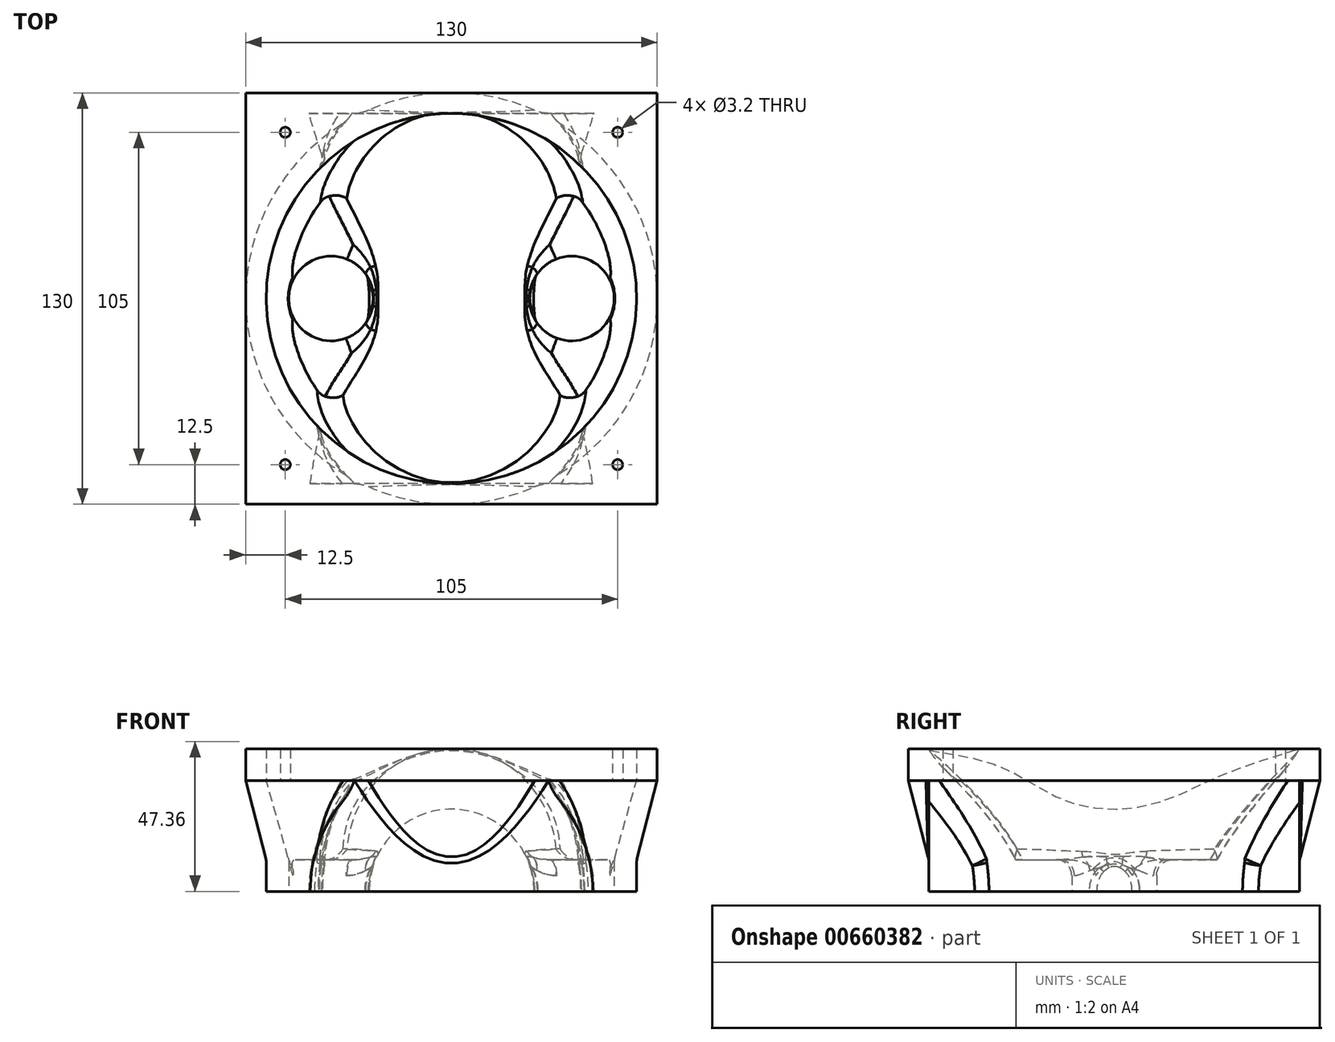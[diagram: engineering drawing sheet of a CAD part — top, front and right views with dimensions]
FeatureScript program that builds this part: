
annotation { "Feature Type Name" : "Feature", "Feature Type Description" : "" }
export const myFeature = defineFeature(function(context is Context, id is Id, definition is map)
    precondition{}
    {
        {
            var Q0;
            Q0=qCreatedBy(makeId("Front.planeOp"),FACE);
            var sketch = newSketch(context, id + "F0", { "sketchPlane" : qUnion([Q0])});
            skPoint(sketch, "E0", {"position": v(56, 0) * mm});
            skPoint(sketch, "E1", {"position": v(65, 35) * mm});
            skLineSegment(sketch, "E2", {"start": v(0, 10) * mm, "end": v(0, 35) * mm});
            skPoint(sketch, "E3", {"position": v(58.5, 35) * mm});
            skPoint(sketch, "E4", {"position": v(-21.4, 10) * mm});
            skLineSegment(sketch, "E5", {"start": v(51.4, 10) * mm, "end": v(53, 10) * mm});
            skLineSegment(sketch, "E6", {"start": v(53, 10) * mm, "end": v(53, 0) * mm});
            skLineSegment(sketch, "E7", {"start": v(58.5, 35) * mm, "end": v(65, 35) * mm});
            skPoint(sketch, "E8", {"position": v(53, 10) * mm});
            skLineSegment(sketch, "E9", {"start": v(58.5, 35) * mm, "end": v(51.4, 10) * mm});
            skLineSegment(sketch, "E10", {"start": v(53, 0) * mm, "end": v(56, 0) * mm});
            skLineSegment(sketch, "E11", {"start": v(65, 35) * mm, "end": v(56, 0) * mm});
            skPoint(sketch, "E12", {"position": v(51.4, 10) * mm});
            skPoint(sketch, "E13", {"position": v(21.4, 10) * mm});
            skLineSegment(sketch, "E14", {"start": v(21.4, 10) * mm, "end": v(23, 10) * mm});
            skCircle(sketch, "E15", {"center": v(0, 10) * mm, "radius": 23 * mm, "construction": true});
            skCircle(sketch, "E16", {"center": v(0, 10) * mm, "radius": 21.4 * mm, "construction": true});
            skLineSegment(sketch, "E17", {"start": v(23, 10) * mm, "end": v(23, 0) * mm});
            skLineSegment(sketch, "E18", {"start": v(23, 0) * mm, "end": v(0, 0) * mm});
            skArc(sketch, "E19", {"start": v(0, 31.4) * mm, "mid": v(15.13, 25.13) * mm, "end": v(21.4, 10) * mm});
            skLineSegment(sketch, "E20", {"start": v(0, 10) * mm, "end": v(0, 0) * mm});
            skLineSegment(sketch, "E21", {"start": v(23, 10) * mm, "end": v(51.4, 10) * mm, "construction": true});
            skPoint(sketch, "E22", {"position": v(37.2, 10) * mm});
            skCircle(sketch, "E23", {"center": v(37.2, 10) * mm, "radius": 14.2 * mm, "construction": true});
            skArc(sketch, "E24", {"start": v(23, 10) * mm, "mid": v(37.2, 24.2) * mm, "end": v(51.4, 10) * mm});
            skLineSegment(sketch, "E25", {"start": v(23, 0) * mm, "end": v(53, 0) * mm});
            skFitSpline(sketch, "E26", {"points": [v(58.5, 35) * mm, v(53.56, 28.48) * mm, v(37.2, 24.2) * mm], "startDerivative": vector(-8.81, -17.66) * mm, "endDerivative": vector(-32.37, -4.71) * mm});
            skSolve(sketch);
        }
        {
            var Q0;
            Q0=makeQuery(id+"F0.imprint","IMPRINT",FACE,{"disambiguationData":[TD([[makeQuery(id+"F0.imprint","IMPRINT",EDGE,{"derivedFrom":sQuery(id+"F0.wireOp",EDGE,"E5")}),1.0]])]});
            var Q1;
            Q1=sQuery(id+"F0.wireOp",EDGE,"E2");
            revolve(context, id + "F1", {"entities" : qUnion([Q0]), "axis" : qUnion([Q1]), "revolveType" : RevolveType.FULL});
        }
        {
            var Q0;
            Q0=qCreatedBy(makeId("Top.planeOp"),FACE);
            var sketch = newSketch(context, id + "F2", { "sketchPlane" : qUnion([Q0])});
            skLineSegment(sketch, "E27.bottom", {"start": v(-50, -12) * mm, "end": v(-26, -12) * mm, "construction": true});
            skLineSegment(sketch, "E27.top", {"start": v(-50, 12) * mm, "end": v(-26, 12) * mm, "construction": true});
            skLineSegment(sketch, "E27.left", {"start": v(-50, -12) * mm, "end": v(-50, 12) * mm, "construction": true});
            skLineSegment(sketch, "E27.right", {"start": v(-26, -12) * mm, "end": v(-26, 12) * mm, "construction": true});
            skLineSegment(sketch, "E28.bottom", {"start": v(-53, -15) * mm, "end": v(-23, -15) * mm});
            skLineSegment(sketch, "E28.top", {"start": v(-53, 15) * mm, "end": v(-23, 15) * mm});
            skLineSegment(sketch, "E28.left", {"start": v(-53, -15) * mm, "end": v(-53, 15) * mm});
            skLineSegment(sketch, "E28.right", {"start": v(-23, -15) * mm, "end": v(-23, 15) * mm});
            skCircle(sketch, "E29", {"center": v(-50, 12) * mm, "radius": 1.6 * mm});
            skCircle(sketch, "E30", {"center": v(-50, -12) * mm, "radius": 1.6 * mm});
            skCircle(sketch, "E31", {"center": v(-26, 12) * mm, "radius": 1.6 * mm});
            skCircle(sketch, "E32", {"center": v(-26, -12) * mm, "radius": 1.6 * mm});
            skCircle(sketch, "E33", {"center": v(-38, 0) * mm, "radius": 13.4 * mm});
            skLineSegment(sketch, "E34", {"start": v(0, 86.14) * mm, "end": v(13.4, 86.14) * mm});
            skLineSegment(sketch, "E35", {"start": v(0, 86.14) * mm, "end": v(0, 121.14) * mm});
            skLineSegment(sketch, "E36", {"start": v(0, 121.14) * mm, "end": v(60, 121.14) * mm});
            skLineSegment(sketch, "E37", {"start": v(13.4, 86.14) * mm, "end": v(60, 121.14) * mm});
            skLineSegment(sketch, "E38.bottom", {"start": v(-60, -60) * mm, "end": v(60, -60) * mm});
            skLineSegment(sketch, "E38.top", {"start": v(-60, 60) * mm, "end": v(60, 60) * mm});
            skLineSegment(sketch, "E38.left", {"start": v(-60, -60) * mm, "end": v(-60, 60) * mm});
            skLineSegment(sketch, "E38.right", {"start": v(60, -60) * mm, "end": v(60, 60) * mm});
            skLineSegment(sketch, "E39.bottom", {"start": v(-52.5, -52.5) * mm, "end": v(52.5, -52.5) * mm, "construction": true});
            skLineSegment(sketch, "E39.top", {"start": v(-52.5, 52.5) * mm, "end": v(52.5, 52.5) * mm, "construction": true});
            skLineSegment(sketch, "E39.left", {"start": v(-52.5, -52.5) * mm, "end": v(-52.5, 52.5) * mm, "construction": true});
            skLineSegment(sketch, "E39.right", {"start": v(52.5, -52.5) * mm, "end": v(52.5, 52.5) * mm, "construction": true});
            skCircle(sketch, "E40", {"center": v(-52.5, 52.5) * mm, "radius": 1.6 * mm});
            skCircle(sketch, "E41", {"center": v(52.5, 52.5) * mm, "radius": 1.6 * mm});
            skCircle(sketch, "E42", {"center": v(52.5, -52.5) * mm, "radius": 1.6 * mm});
            skCircle(sketch, "E43", {"center": v(-52.5, -52.5) * mm, "radius": 1.6 * mm});
            skCircle(sketch, "E44", {"center": v(0, 0) * mm, "radius": 58.5 * mm});
            skLineSegment(sketch, "E45.bottom", {"start": v(-65, -65) * mm, "end": v(65, -65) * mm});
            skLineSegment(sketch, "E45.top", {"start": v(-65, 65) * mm, "end": v(65, 65) * mm});
            skLineSegment(sketch, "E45.left", {"start": v(-65, -65) * mm, "end": v(-65, 65) * mm});
            skLineSegment(sketch, "E45.right", {"start": v(65, -65) * mm, "end": v(65, 65) * mm});
            skLineSegment(sketch, "E46.bottom", {"start": v(26, -12) * mm, "end": v(50, -12) * mm, "construction": true});
            skLineSegment(sketch, "E46.top", {"start": v(26, 12) * mm, "end": v(50, 12) * mm, "construction": true});
            skLineSegment(sketch, "E46.left", {"start": v(26, -12) * mm, "end": v(26, 12) * mm, "construction": true});
            skLineSegment(sketch, "E46.right", {"start": v(50, -12) * mm, "end": v(50, 12) * mm, "construction": true});
            skLineSegment(sketch, "E47.bottom", {"start": v(23, -15) * mm, "end": v(53, -15) * mm});
            skLineSegment(sketch, "E47.top", {"start": v(23, 15) * mm, "end": v(53, 15) * mm});
            skLineSegment(sketch, "E47.left", {"start": v(23, -15) * mm, "end": v(23, 15) * mm});
            skLineSegment(sketch, "E47.right", {"start": v(53, -15) * mm, "end": v(53, 15) * mm});
            skCircle(sketch, "E48", {"center": v(26, 12) * mm, "radius": 1.6 * mm});
            skCircle(sketch, "E49", {"center": v(26, -12) * mm, "radius": 1.6 * mm});
            skCircle(sketch, "E50", {"center": v(50, 12) * mm, "radius": 1.6 * mm});
            skCircle(sketch, "E51", {"center": v(50, -12) * mm, "radius": 1.6 * mm});
            skCircle(sketch, "E52", {"center": v(38, 0) * mm, "radius": 13.4 * mm});
            skCircle(sketch, "E53", {"center": v(0, -1.14) * mm, "radius": 55.4 * mm, "construction": true});
            skPoint(sketch, "E54.centerSnap0", {"position": v(0, 52.5) * mm});
            skLineSegment(sketch, "E55", {"start": v(0, -65) * mm, "end": v(0, 65) * mm});
            skPoint(sketch, "E56", {"position": v(-15.07, 31.68) * mm});
            skCircle(sketch, "E57", {"center": v(-38, 0) * mm, "radius": 20 * mm, "construction": true});
            skArc(sketch, "E58", {"start": v(-29.98, 45.45) * mm, "mid": v(-37.4, 30.88) * mm, "end": v(-28.14, 17.4) * mm});
            skCircle(sketch, "E59", {"center": v(38, 0) * mm, "radius": 20 * mm, "construction": true});
            skArc(sketch, "E60", {"start": v(28.14, 17.4) * mm, "mid": v(37.4, 30.88) * mm, "end": v(29.98, 45.45) * mm});
            skArc(sketch, "E61", {"start": v(-28.14, -17.4) * mm, "mid": v(-37.97, -32.03) * mm, "end": v(-29.98, -47.73) * mm});
            skArc(sketch, "E62", {"start": v(29.98, -47.73) * mm, "mid": v(38.6, -31.99) * mm, "end": v(28.14, -17.4) * mm});
            skArc(sketch, "E63", {"start": v(-29.98, 45.45) * mm, "mid": v(0, 54.45) * mm, "end": v(29.98, 45.45) * mm});
            skArc(sketch, "E64", {"start": v(-29.98, -47.73) * mm, "mid": v(0, -56.37) * mm, "end": v(29.98, -47.73) * mm});
            skArc(sketch, "E65", {"start": v(-28.14, 17.4) * mm, "mid": v(-18, 0) * mm, "end": v(-28.14, -17.4) * mm});
            skArc(sketch, "E66", {"start": v(28.14, 17.4) * mm, "mid": v(18, 0) * mm, "end": v(28.14, -17.4) * mm});
            skPoint(sketch, "E67.orphan", {"position": v(0, 4.6) * mm});
            skSolve(sketch);
        }
        {
            var Q0;
            Q0=makeQuery(id+"F2.imprint","IMPRINT",FACE,{"disambiguationData":[TD([[makeQuery(id+"F2.imprint","IMPRINT",EDGE,{"derivedFrom":sQuery(id+"F2.wireOp",EDGE,"E28.bottom")}),1.0]])]});
            var Q1;
            Q1=makeQuery(id+"F2.imprint","IMPRINT",FACE,{"disambiguationData":[TD([[makeQuery(id+"F2.imprint","IMPRINT",EDGE,{"derivedFrom":sQuery(id+"F2.wireOp",EDGE,"E47.bottom")}),1.0]])]});
            var Q2;
            Q2=makeQuery(id+"F2.imprint","IMPRINT",FACE,{"disambiguationData":[TD([[makeQuery(id+"F2.imprint","IMPRINT",EDGE,{"derivedFrom":sQuery(id+"F2.wireOp",EDGE,"E50")}),1.0]])]});
            var Q3;
            Q3=makeQuery(id+"F2.imprint","IMPRINT",FACE,{"disambiguationData":[TD([[makeQuery(id+"F2.imprint","IMPRINT",EDGE,{"derivedFrom":sQuery(id+"F2.wireOp",EDGE,"E51")}),1.0]])]});
            var Q4;
            Q4=makeQuery(id+"F2.imprint","IMPRINT",FACE,{"disambiguationData":[TD([[makeQuery(id+"F2.imprint","IMPRINT",EDGE,{"derivedFrom":sQuery(id+"F2.wireOp",EDGE,"E29")}),1.0]])]});
            var Q5;
            Q5=makeQuery(id+"F2.imprint","IMPRINT",FACE,{"disambiguationData":[TD([[makeQuery(id+"F2.imprint","IMPRINT",EDGE,{"derivedFrom":sQuery(id+"F2.wireOp",EDGE,"E30")}),1.0]])]});
            var Q6;
            Q6=makeQuery(id+"F2.imprint","IMPRINT",FACE,{"disambiguationData":[TD([[makeQuery(id+"F2.imprint","IMPRINT",EDGE,{"derivedFrom":sQuery(id+"F2.wireOp",EDGE,"E28.bottom")}),-1.0]])]});
            var Q7;
            {var subQ0=sQuery(id+"F2.wireOp",EDGE,"E65");var subQ1=sQuery(id+"F2.wireOp",EDGE,"E28.right");var subQ2=makeQuery(id+"F2.imprint","INTERSECT",VERTEX,{"disambiguationData":[OD(0.0)],"derivedFrom":[subQ1,subQ0]});Q7=makeQuery(id+"F2.imprint","IMPRINT",FACE,{"disambiguationData":[TD([[makeQuery(id+"F2.imprint","IMPRINT",EDGE,{"disambiguationData":[TD([[subQ2,-1.0]])],"derivedFrom":subQ1}),-1.0]])]});}
            var Q8;
            {var subQ0=sQuery(id+"F2.wireOp",EDGE,"E28.right");var subQ1=sQuery(id+"F2.wireOp",EDGE,"E28.top");var subQ2=makeQuery(id+"F2.imprint","INTERSECT",VERTEX,{"derivedFrom":[subQ1,subQ0]});Q8=makeQuery(id+"F2.imprint","IMPRINT",FACE,{"disambiguationData":[TD([[makeQuery(id+"F2.imprint","IMPRINT",EDGE,{"disambiguationData":[TD([[subQ2,1.0]])],"derivedFrom":subQ1}),-1.0]])]});}
            var Q9;
            {var subQ5=sQuery(id+"F2.wireOp",EDGE,"E28.left");Q9=makeQuery(id+"F2.imprint","IMPRINT",FACE,{"disambiguationData":[TD([[makeQuery(id+"F2.imprint","IMPRINT",EDGE,{"derivedFrom":subQ5}),-1.0]])]});}
            var Q10;
            {var subQ1=sQuery(id+"F2.wireOp",EDGE,"E60");Q10=makeQuery(id+"F2.imprint","IMPRINT",FACE,{"disambiguationData":[TD([[makeQuery(id+"F2.imprint","IMPRINT",EDGE,{"derivedFrom":subQ1}),1.0]])]});}
            var Q11;
            {var subQ10=sQuery(id+"F2.wireOp",EDGE,"E47.right");Q11=makeQuery(id+"F2.imprint","IMPRINT",FACE,{"disambiguationData":[TD([[makeQuery(id+"F2.imprint","IMPRINT",EDGE,{"derivedFrom":subQ10}),-1.0]])]});}
            var Q12;
            {var subQ0=sQuery(id+"F2.wireOp",EDGE,"E66");var subQ1=sQuery(id+"F2.wireOp",EDGE,"E47.left");var subQ2=makeQuery(id+"F2.imprint","INTERSECT",VERTEX,{"disambiguationData":[OD(0.0)],"derivedFrom":[subQ1,subQ0]});Q12=makeQuery(id+"F2.imprint","IMPRINT",FACE,{"disambiguationData":[TD([[makeQuery(id+"F2.imprint","IMPRINT",EDGE,{"disambiguationData":[TD([[subQ2,-1.0]])],"derivedFrom":subQ1}),1.0]])]});}
            var Q13;
            {var subQ5=sQuery(id+"F2.wireOp",EDGE,"E47.right");Q13=makeQuery(id+"F2.imprint","IMPRINT",FACE,{"disambiguationData":[TD([[makeQuery(id+"F2.imprint","IMPRINT",EDGE,{"derivedFrom":subQ5}),1.0]])]});}
            var Q14;
            {var subQ0=sQuery(id+"F2.wireOp",EDGE,"E47.left");var subQ1=sQuery(id+"F2.wireOp",EDGE,"E47.top");var subQ2=makeQuery(id+"F2.imprint","INTERSECT",VERTEX,{"derivedFrom":[subQ1,subQ0]});Q14=makeQuery(id+"F2.imprint","IMPRINT",FACE,{"disambiguationData":[TD([[makeQuery(id+"F2.imprint","IMPRINT",EDGE,{"disambiguationData":[TD([[subQ2,-1.0]])],"derivedFrom":subQ1}),-1.0]])]});}
            var Q15;
            Q15=makeQuery(id+"F2.imprint","IMPRINT",FACE,{"disambiguationData":[TD([[makeQuery(id+"F2.imprint","IMPRINT",EDGE,{"derivedFrom":sQuery(id+"F2.wireOp",EDGE,"E31")}),1.0]])]});
            var Q16;
            Q16=makeQuery(id+"F2.imprint","IMPRINT",FACE,{"disambiguationData":[TD([[makeQuery(id+"F2.imprint","IMPRINT",EDGE,{"derivedFrom":sQuery(id+"F2.wireOp",EDGE,"E32")}),1.0]])]});
            var Q17;
            Q17=makeQuery(id+"F2.imprint","IMPRINT",FACE,{"disambiguationData":[TD([[makeQuery(id+"F2.imprint","IMPRINT",EDGE,{"derivedFrom":sQuery(id+"F2.wireOp",EDGE,"E49")}),1.0]])]});
            var Q18;
            Q18=makeQuery(id+"F2.imprint","IMPRINT",FACE,{"disambiguationData":[TD([[makeQuery(id+"F2.imprint","IMPRINT",EDGE,{"derivedFrom":sQuery(id+"F2.wireOp",EDGE,"E48")}),1.0]])]});
            extrude(context, id + "F3", {"entities" : qUnion([Q0, Q1, Q2, Q3, Q4, Q5, Q6, Q7, Q8, Q9, Q10, Q11, Q12, Q13, Q14, Q15, Q16, Q17, Q18]), "operationType" : NewBodyOperationType.ADD, "depth" : 10 * mm, "offsetDistance" : 25 * mm});
        }
        {
            var Q0;
            Q0=makeQuery(id+"F2.imprint","IMPRINT",FACE,{"disambiguationData":[TD([[makeQuery(id+"F2.imprint","IMPRINT",EDGE,{"derivedFrom":sQuery(id+"F2.wireOp",EDGE,"E38.bottom")}),1.0]])]});
            var Q1;
            Q1=makeQuery(id+"F2.imprint","IMPRINT",FACE,{"disambiguationData":[TD([[makeQuery(id+"F2.imprint","IMPRINT",EDGE,{"derivedFrom":sQuery(id+"F2.wireOp",EDGE,"E38.bottom")}),-1.0]])]});
            extrude(context, id + "F4", {"entities" : qUnion([Q0, Q1]), "operationType" : NewBodyOperationType.ADD, "depth" : 45 * mm, "offsetDistance" : 25 * mm, "hasSecondDirection" : true, "secondDirectionOppositeDirection" : false, "secondDirectionDepth" : 35 * mm});
        }
        {
            var Q0;
            Q0=qCreatedBy(makeId("Right.planeOp"),FACE);
            var sketch = newSketch(context, id + "F5", { "sketchPlane" : qUnion([Q0])});
            skLineSegment(sketch, "E68", {"start": v(0, 0) * mm, "end": v(-58.54, 0) * mm});
            skLineSegment(sketch, "E69", {"start": v(-58.54, 0) * mm, "end": v(-58.54, 44.62) * mm});
            skLineSegment(sketch, "E70", {"start": v(0, 0) * mm, "end": v(58.52, 0) * mm});
            skLineSegment(sketch, "E71", {"start": v(58.52, 0) * mm, "end": v(58.52, 45.07) * mm});
            skFitSpline(sketch, "E72", {"points": [v(-58.54, 44.62) * mm, v(-34.86, 38.92) * mm, v(-16.7, 29.15) * mm, v(0, 25.97) * mm, v(15.9, 28.73) * mm, v(33.95, 36.7) * mm, v(58.52, 45.07) * mm], "startDerivative": vector(136.5, -21.55) * mm, "endDerivative": vector(136.53, 41.7) * mm});
            skSolve(sketch);
        }
        {
            var Q0;
            Q0=makeQuery(id+"F5.imprint","IMPRINT",FACE,{"disambiguationData":[TD([[makeQuery(id+"F5.imprint","IMPRINT",EDGE,{"derivedFrom":sQuery(id+"F5.wireOp",EDGE,"E68")}),-1.0]])]});
            var Q1;
            Q1=sQuery(id+"F5.wireOp",EDGE,"E68");
            revolve(context, id + "F6", {"operationType" : NewBodyOperationType.ADD, "entities" : qUnion([Q0]), "axis" : qUnion([Q1]), "revolveType" : RevolveType.SYMMETRIC, "angle" : 180 * degree});
        }
        {
            var Q0;
            Q0=makeQuery(id+"F6.boolean.opBoolean","INTERSECT",EDGE,{"disambiguationData":[OD(0.0)],"derivedFrom":[makeQuery(id+"F3.opExtrude","CAP_FACE",FACE,{"disambiguationData":[OSD([sQuery(id+"F2.wireOp",EDGE,"E33"),sQuery(id+"F2.wireOp",EDGE,"E44"),sQuery(id+"F2.wireOp",EDGE,"E52")])],"isStart":false}),makeQuery(id+"F6.opRevolve","SWEPT_FACE",FACE,{"disambiguationData":[OSD([sQuery(id+"F5.wireOp",EDGE,"E72")])]})]});
            var Q1;
            Q1=makeQuery(id+"F6.boolean.opBoolean","INTERSECT",EDGE,{"disambiguationData":[OD(1.0)],"derivedFrom":[makeQuery(id+"F3.opExtrude","CAP_FACE",FACE,{"disambiguationData":[OSD([sQuery(id+"F2.wireOp",EDGE,"E33"),sQuery(id+"F2.wireOp",EDGE,"E44"),sQuery(id+"F2.wireOp",EDGE,"E52")])],"isStart":false}),makeQuery(id+"F6.opRevolve","SWEPT_FACE",FACE,{"disambiguationData":[OSD([sQuery(id+"F5.wireOp",EDGE,"E72")])]})]});
            var Q2;
            Q2=makeQuery(id+"F6.boolean.opBoolean","INTERSECT",EDGE,{"disambiguationData":[OD(0.0)],"derivedFrom":[makeQuery(id+"F1.opRevolve","SWEPT_FACE",FACE,{"disambiguationData":[OSD([sQuery(id+"F0.wireOp",EDGE,"E9")])]}),makeQuery(id+"F6.opRevolve","SWEPT_FACE",FACE,{"disambiguationData":[OSD([sQuery(id+"F5.wireOp",EDGE,"E72")])]})]});
            var Q3;
            Q3=makeQuery(id+"F6.boolean.opBoolean","INTERSECT",EDGE,{"disambiguationData":[OD(1.0)],"derivedFrom":[makeQuery(id+"F1.opRevolve","SWEPT_FACE",FACE,{"disambiguationData":[OSD([sQuery(id+"F0.wireOp",EDGE,"E9")])]}),makeQuery(id+"F6.opRevolve","SWEPT_FACE",FACE,{"disambiguationData":[OSD([sQuery(id+"F5.wireOp",EDGE,"E72")])]})]});
            var Q4;
            Q4=makeQuery(id+"F6.boolean.opBoolean","INTERSECT",EDGE,{"disambiguationData":[OD(3.0)],"derivedFrom":[makeQuery(id+"F1.opRevolve","SWEPT_FACE",FACE,{"disambiguationData":[OSD([sQuery(id+"F0.wireOp",EDGE,"E9")])]}),makeQuery(id+"F6.opRevolve","SWEPT_FACE",FACE,{"disambiguationData":[OSD([sQuery(id+"F5.wireOp",EDGE,"E72")])]})]});
            fillet(context, id + "F7", {"entities" : qUnion([Q0, Q1, Q2, Q3, Q4]), "radius" : 5 * mm, "tangentPropagation" : true, "allowEdgeOverflow" : false});
        }
        {
            var Q0;
            Q0=makeQuery(id+"F6.boolean.opBoolean","INTERSECT",EDGE,{"disambiguationData":[OD(2.0)],"derivedFrom":[makeQuery(id+"F1.opRevolve","SWEPT_FACE",FACE,{"disambiguationData":[OSD([sQuery(id+"F0.wireOp",EDGE,"E11")])]}),makeQuery(id+"F6.opRevolve","SWEPT_FACE",FACE,{"disambiguationData":[OSD([sQuery(id+"F5.wireOp",EDGE,"E72")])]})]});
            var Q1;
            Q1=makeQuery(id+"F6.boolean.opBoolean","INTERSECT",EDGE,{"disambiguationData":[OD(1.0)],"derivedFrom":[makeQuery(id+"F3.opExtrude","SWEPT_FACE",FACE,{"disambiguationData":[OSD([sQuery(id+"F2.wireOp",EDGE,"E44")])]}),makeQuery(id+"F6.opRevolve","SWEPT_FACE",FACE,{"disambiguationData":[OSD([sQuery(id+"F5.wireOp",EDGE,"E72")])]})]});
            var Q2;
            Q2=makeQuery(id+"F6.boolean.opBoolean","INTERSECT",EDGE,{"disambiguationData":[OD(1.0)],"derivedFrom":[makeQuery(id+"F1.opRevolve","SWEPT_FACE",FACE,{"disambiguationData":[OSD([sQuery(id+"F0.wireOp",EDGE,"E11")])]}),makeQuery(id+"F6.opRevolve","SWEPT_FACE",FACE,{"disambiguationData":[OSD([sQuery(id+"F5.wireOp",EDGE,"E72")])]})]});
            var Q3;
            Q3=makeQuery(id+"F6.boolean.opBoolean","INTERSECT",EDGE,{"disambiguationData":[OD(2.0)],"derivedFrom":[makeQuery(id+"F3.opExtrude","SWEPT_FACE",FACE,{"disambiguationData":[OSD([sQuery(id+"F2.wireOp",EDGE,"E44")])]}),makeQuery(id+"F6.opRevolve","SWEPT_FACE",FACE,{"disambiguationData":[OSD([sQuery(id+"F5.wireOp",EDGE,"E72")])]})]});
            var Q4;
            Q4=makeQuery(id+"F6.boolean.opBoolean","INTERSECT",EDGE,{"disambiguationData":[OD(3.0)],"derivedFrom":[makeQuery(id+"F3.opExtrude","SWEPT_FACE",FACE,{"disambiguationData":[OSD([sQuery(id+"F2.wireOp",EDGE,"E44")])]}),makeQuery(id+"F6.opRevolve","SWEPT_FACE",FACE,{"disambiguationData":[OSD([sQuery(id+"F5.wireOp",EDGE,"E72")])]})]});
            var Q5;
            Q5=makeQuery(id+"F6.boolean.opBoolean","INTERSECT",EDGE,{"disambiguationData":[OD(0.0)],"derivedFrom":[makeQuery(id+"F3.opExtrude","SWEPT_FACE",FACE,{"disambiguationData":[OSD([sQuery(id+"F2.wireOp",EDGE,"E44")])]}),makeQuery(id+"F6.opRevolve","SWEPT_FACE",FACE,{"disambiguationData":[OSD([sQuery(id+"F5.wireOp",EDGE,"E72")])]})]});
            var Q6;
            Q6=makeQuery(id+"F6.boolean.opBoolean","INTERSECT",EDGE,{"disambiguationData":[OD(0.0)],"derivedFrom":[makeQuery(id+"F1.opRevolve","SWEPT_FACE",FACE,{"disambiguationData":[OSD([sQuery(id+"F0.wireOp",EDGE,"E11")])]}),makeQuery(id+"F6.opRevolve","SWEPT_FACE",FACE,{"disambiguationData":[OSD([sQuery(id+"F5.wireOp",EDGE,"E72")])]})]});
            var Q7;
            Q7=makeQuery(id+"F6.boolean.opBoolean","INTERSECT",EDGE,{"disambiguationData":[OD(3.0)],"derivedFrom":[makeQuery(id+"F1.opRevolve","SWEPT_FACE",FACE,{"disambiguationData":[OSD([sQuery(id+"F0.wireOp",EDGE,"E11")])]}),makeQuery(id+"F6.opRevolve","SWEPT_FACE",FACE,{"disambiguationData":[OSD([sQuery(id+"F5.wireOp",EDGE,"E72")])]})]});
            var Q8;
            Q8=makeQuery(id+"F6.boolean.opBoolean","SPLIT",EDGE,{"disambiguationData":[OD(0.0)],"derivedFrom":makeQuery(id+"F3.boolean.opBoolean","INTERSECT",EDGE,{"derivedFrom":[makeQuery(id+"F1.opRevolve","SWEPT_FACE",FACE,{"disambiguationData":[OSD([sQuery(id+"F0.wireOp",EDGE,"E11")])]}),makeQuery(id+"F3.opExtrude","SWEPT_FACE",FACE,{"disambiguationData":[OSD([sQuery(id+"F2.wireOp",EDGE,"E44")])]})]})});
            var Q9;
            Q9=makeQuery(id+"F6.boolean.opBoolean","SPLIT",EDGE,{"disambiguationData":[OD(1.0)],"derivedFrom":makeQuery(id+"F3.boolean.opBoolean","INTERSECT",EDGE,{"derivedFrom":[makeQuery(id+"F1.opRevolve","SWEPT_FACE",FACE,{"disambiguationData":[OSD([sQuery(id+"F0.wireOp",EDGE,"E11")])]}),makeQuery(id+"F3.opExtrude","SWEPT_FACE",FACE,{"disambiguationData":[OSD([sQuery(id+"F2.wireOp",EDGE,"E44")])]})]})});
            fillet(context, id + "F8", {"entities" : qUnion([Q0, Q1, Q2, Q3, Q4, Q5, Q6, Q7, Q8, Q9]), "radius" : 5 * mm, "tangentPropagation" : true, "allowEdgeOverflow" : false});
        }
        {
            var Q0;
            Q0=makeQuery(id+"F6.boolean.opBoolean","INTERSECT",EDGE,{"derivedFrom":[makeQuery(id+"F1.opRevolve","SWEPT_FACE",FACE,{"disambiguationData":[OSD([sQuery(id+"F0.wireOp",EDGE,"E11")])]}),makeQuery(id+"F6.opRevolve","SWEPT_FACE",FACE,{"disambiguationData":[OSD([sQuery(id+"F5.wireOp",EDGE,"E69")])]})]});
            var Q1;
            Q1=makeQuery(id+"F6.boolean.opBoolean","INTERSECT",EDGE,{"derivedFrom":[makeQuery(id+"F1.opRevolve","SWEPT_FACE",FACE,{"disambiguationData":[OSD([sQuery(id+"F0.wireOp",EDGE,"E11")])]}),makeQuery(id+"F6.opRevolve","SWEPT_FACE",FACE,{"disambiguationData":[OSD([sQuery(id+"F5.wireOp",EDGE,"E71")])]})]});
            fillet(context, id + "F9", {"entities" : qUnion([Q0, Q1]), "radius" : 8 * mm, "tangentPropagation" : true, "allowEdgeOverflow" : false});
        }
        {
            var Q0;
            {var subQ0=sQuery(id+"F2.wireOp",EDGE,"E33");Q0=makeQuery(id+"F7.opFillet","BLEND_EDGE",EDGE,{"blendedFrom":[makeQuery(id+"F6.boolean.opBoolean","INTERSECT",EDGE,{"disambiguationData":[OD(0.0)],"derivedFrom":[makeQuery(id+"F3.opExtrude","CAP_FACE",FACE,{"disambiguationData":[OSD([subQ0,sQuery(id+"F2.wireOp",EDGE,"E44"),sQuery(id+"F2.wireOp",EDGE,"E52")])],"isStart":false}),makeQuery(id+"F6.opRevolve","SWEPT_FACE",FACE,{"disambiguationData":[OSD([sQuery(id+"F5.wireOp",EDGE,"E72")])]})]}),makeQuery(id+"F3.opExtrude","SWEPT_FACE",FACE,{"disambiguationData":[OSD([subQ0])]})],"blendedInto":[makeQuery(id+"F3.opExtrude","SWEPT_FACE",FACE,{"disambiguationData":[OSD([subQ0])]})]});}
            var Q1;
            {var subQ0=sQuery(id+"F2.wireOp",EDGE,"E52");Q1=makeQuery(id+"F7.opFillet","BLEND_EDGE",EDGE,{"blendedFrom":[makeQuery(id+"F6.boolean.opBoolean","INTERSECT",EDGE,{"disambiguationData":[OD(1.0)],"derivedFrom":[makeQuery(id+"F3.opExtrude","CAP_FACE",FACE,{"disambiguationData":[OSD([sQuery(id+"F2.wireOp",EDGE,"E33"),sQuery(id+"F2.wireOp",EDGE,"E44"),subQ0])],"isStart":false}),makeQuery(id+"F6.opRevolve","SWEPT_FACE",FACE,{"disambiguationData":[OSD([sQuery(id+"F5.wireOp",EDGE,"E72")])]})]}),makeQuery(id+"F3.opExtrude","SWEPT_FACE",FACE,{"disambiguationData":[OSD([subQ0])]})],"blendedInto":[makeQuery(id+"F3.opExtrude","SWEPT_FACE",FACE,{"disambiguationData":[OSD([subQ0])]})]});}
            fillet(context, id + "F10", {"entities" : qUnion([Q0, Q1]), "radius" : 5 * mm, "tangentPropagation" : true, "allowEdgeOverflow" : false});
        }
        {
            var Q0;
            Q0=makeQuery(id+"F6.boolean.opBoolean","INTERSECT",EDGE,{"derivedFrom":[makeQuery(id+"F3.opExtrude","SWEPT_FACE",FACE,{"disambiguationData":[OSD([sQuery(id+"F2.wireOp",EDGE,"E33")])]}),makeQuery(id+"F6.opRevolve","SWEPT_FACE",FACE,{"disambiguationData":[OSD([sQuery(id+"F5.wireOp",EDGE,"E72")])]})]});
            var Q1;
            Q1=makeQuery(id+"F6.boolean.opBoolean","INTERSECT",EDGE,{"derivedFrom":[makeQuery(id+"F3.opExtrude","SWEPT_FACE",FACE,{"disambiguationData":[OSD([sQuery(id+"F2.wireOp",EDGE,"E52")])]}),makeQuery(id+"F6.opRevolve","SWEPT_FACE",FACE,{"disambiguationData":[OSD([sQuery(id+"F5.wireOp",EDGE,"E72")])]})]});
            var Q2;
            {var subQ0=sQuery(id+"F2.wireOp",EDGE,"E52");Q2=makeQuery(id+"F10.opFillet","TWEAK_EDGE",EDGE,{"derivedFrom":[makeQuery(id+"F3.boolean.opBoolean","TWEAK_VERTEX",VERTEX,{"disambiguationData":[OD(0.0)],"derivedFrom":[makeQuery(id+"F1.opRevolve","SWEPT_FACE",FACE,{"disambiguationData":[OSD([sQuery(id+"F0.wireOp",EDGE,"E9")])]}),makeQuery(id+"F3.opExtrude","CAP_FACE",FACE,{"disambiguationData":[OSD([sQuery(id+"F2.wireOp",EDGE,"E33"),sQuery(id+"F2.wireOp",EDGE,"E44"),subQ0])],"isStart":false}),makeQuery(id+"F3.opExtrude","SWEPT_FACE",FACE,{"disambiguationData":[OSD([subQ0])]})]})]});}
            var Q3;
            {var subQ0=sQuery(id+"F2.wireOp",EDGE,"E33");Q3=makeQuery(id+"F10.opFillet","TWEAK_EDGE",EDGE,{"derivedFrom":[makeQuery(id+"F3.boolean.opBoolean","TWEAK_VERTEX",VERTEX,{"disambiguationData":[OD(0.0)],"derivedFrom":[makeQuery(id+"F1.opRevolve","SWEPT_FACE",FACE,{"disambiguationData":[OSD([sQuery(id+"F0.wireOp",EDGE,"E9")])]}),makeQuery(id+"F3.opExtrude","SWEPT_FACE",FACE,{"disambiguationData":[OSD([subQ0])]}),makeQuery(id+"F3.opExtrude","CAP_FACE",FACE,{"disambiguationData":[OSD([subQ0,sQuery(id+"F2.wireOp",EDGE,"E44"),sQuery(id+"F2.wireOp",EDGE,"E52")])],"isStart":false})]})]});}
            fillet(context, id + "F11", {"entities" : qUnion([Q0, Q1, Q2, Q3]), "radius" : 5 * mm, "tangentPropagation" : true, "allowEdgeOverflow" : false});
        }
    });
